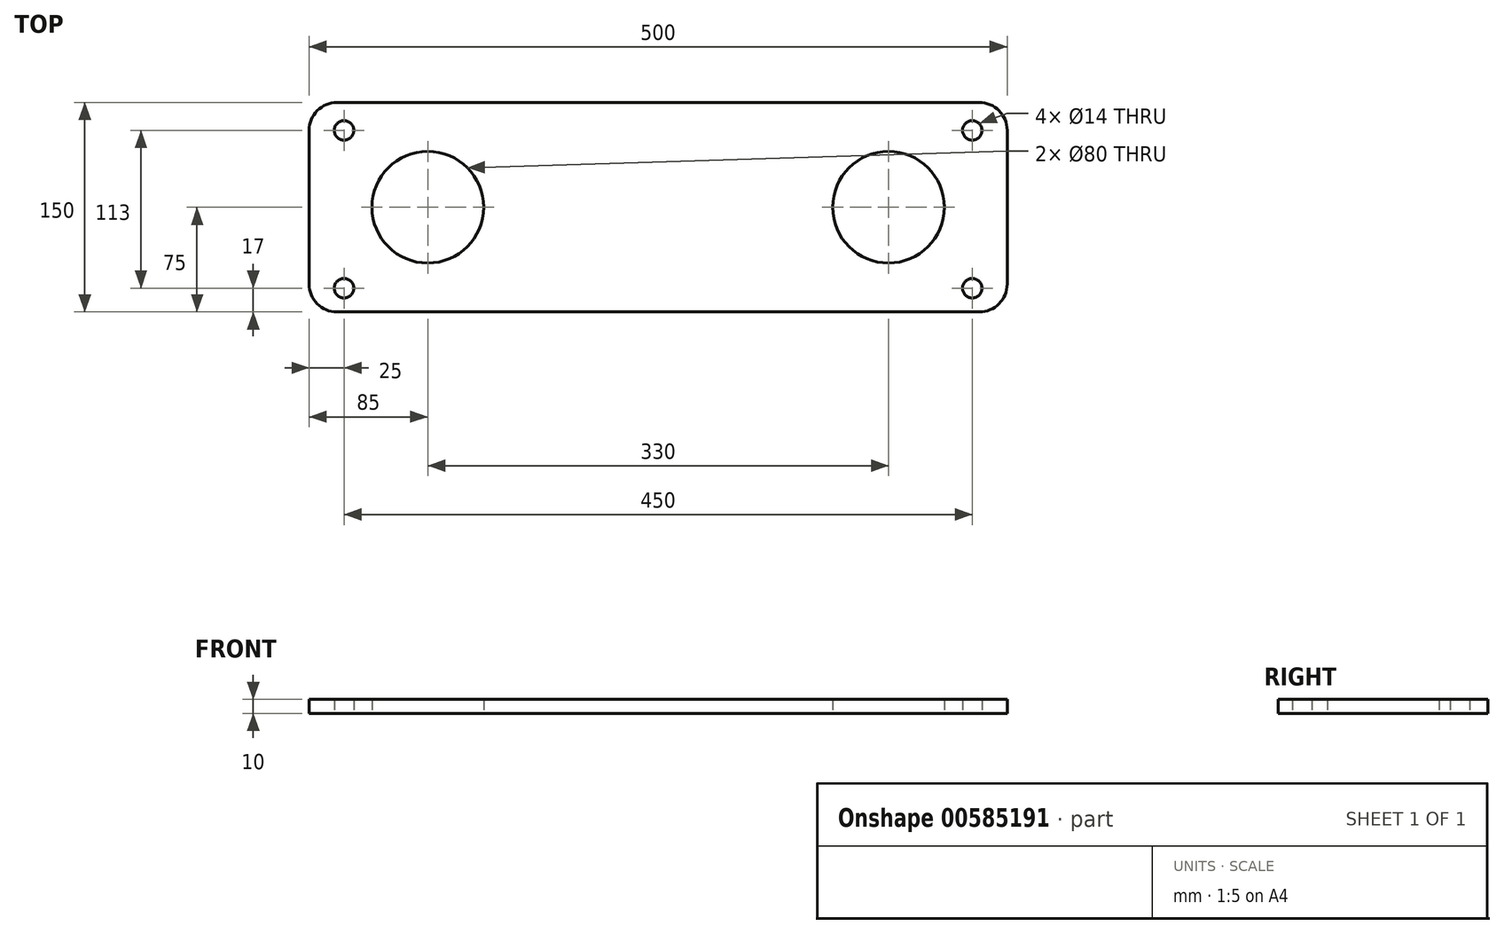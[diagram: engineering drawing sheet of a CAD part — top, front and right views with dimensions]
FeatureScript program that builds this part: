
annotation { "Feature Type Name" : "Feature", "Feature Type Description" : "" }
export const myFeature = defineFeature(function(context is Context, id is Id, definition is map)
    precondition{}
    {
        {
            var Q0;
            Q0=qCreatedBy(makeId("Top.planeOp"),FACE);
            var sketch = newSketch(context, id + "F0", { "sketchPlane" : qUnion([Q0])});
            skLineSegment(sketch, "E0.bottom", {"start": v(-230, 75) * mm, "end": v(230, 75) * mm});
            skLineSegment(sketch, "E0.top", {"start": v(-230, -75) * mm, "end": v(230, -75) * mm});
            skLineSegment(sketch, "E0.left", {"start": v(-250, 55) * mm, "end": v(-250, -55) * mm});
            skLineSegment(sketch, "E0.right", {"start": v(250, 55) * mm, "end": v(250, -55) * mm});
            skCircle(sketch, "E1", {"center": v(-165, 0) * mm, "radius": 40 * mm});
            skCircle(sketch, "E2", {"center": v(165, 0) * mm, "radius": 40 * mm});
            skPoint(sketch, "E3.visualSharp", {"position": v(-250, -75) * mm});
            skArc(sketch, "E3.filletArc", {"start": v(-250, -55) * mm, "mid": v(-244.14, -69.14) * mm, "end": v(-230, -75) * mm});
            skPoint(sketch, "E4.visualSharp", {"position": v(250, -75) * mm});
            skArc(sketch, "E4.filletArc", {"start": v(230, -75) * mm, "mid": v(244.14, -69.14) * mm, "end": v(250, -55) * mm});
            skPoint(sketch, "E5.visualSharp", {"position": v(250, 75) * mm});
            skArc(sketch, "E5.filletArc", {"start": v(250, 55) * mm, "mid": v(244.14, 69.14) * mm, "end": v(230, 75) * mm});
            skPoint(sketch, "E6.visualSharp", {"position": v(-250, 75) * mm});
            skArc(sketch, "E6.filletArc", {"start": v(-230, 75) * mm, "mid": v(-244.14, 69.14) * mm, "end": v(-250, 55) * mm});
            skCircle(sketch, "E7", {"center": v(-225, 55) * mm, "radius": 7 * mm});
            skCircle(sketch, "E8", {"center": v(-225, -58) * mm, "radius": 7 * mm});
            skCircle(sketch, "E9", {"center": v(225, -58) * mm, "radius": 7 * mm});
            skCircle(sketch, "E10", {"center": v(225, 55) * mm, "radius": 7 * mm});
            skSolve(sketch);
        }
        {
            var Q0;
            Q0=qSketchRegion(id+"F0",true);
            extrude(context, id + "F1", {"entities" : qUnion([Q0]), "depth" : 10 * mm, "offsetDistance" : 25 * mm});
        }
    });
